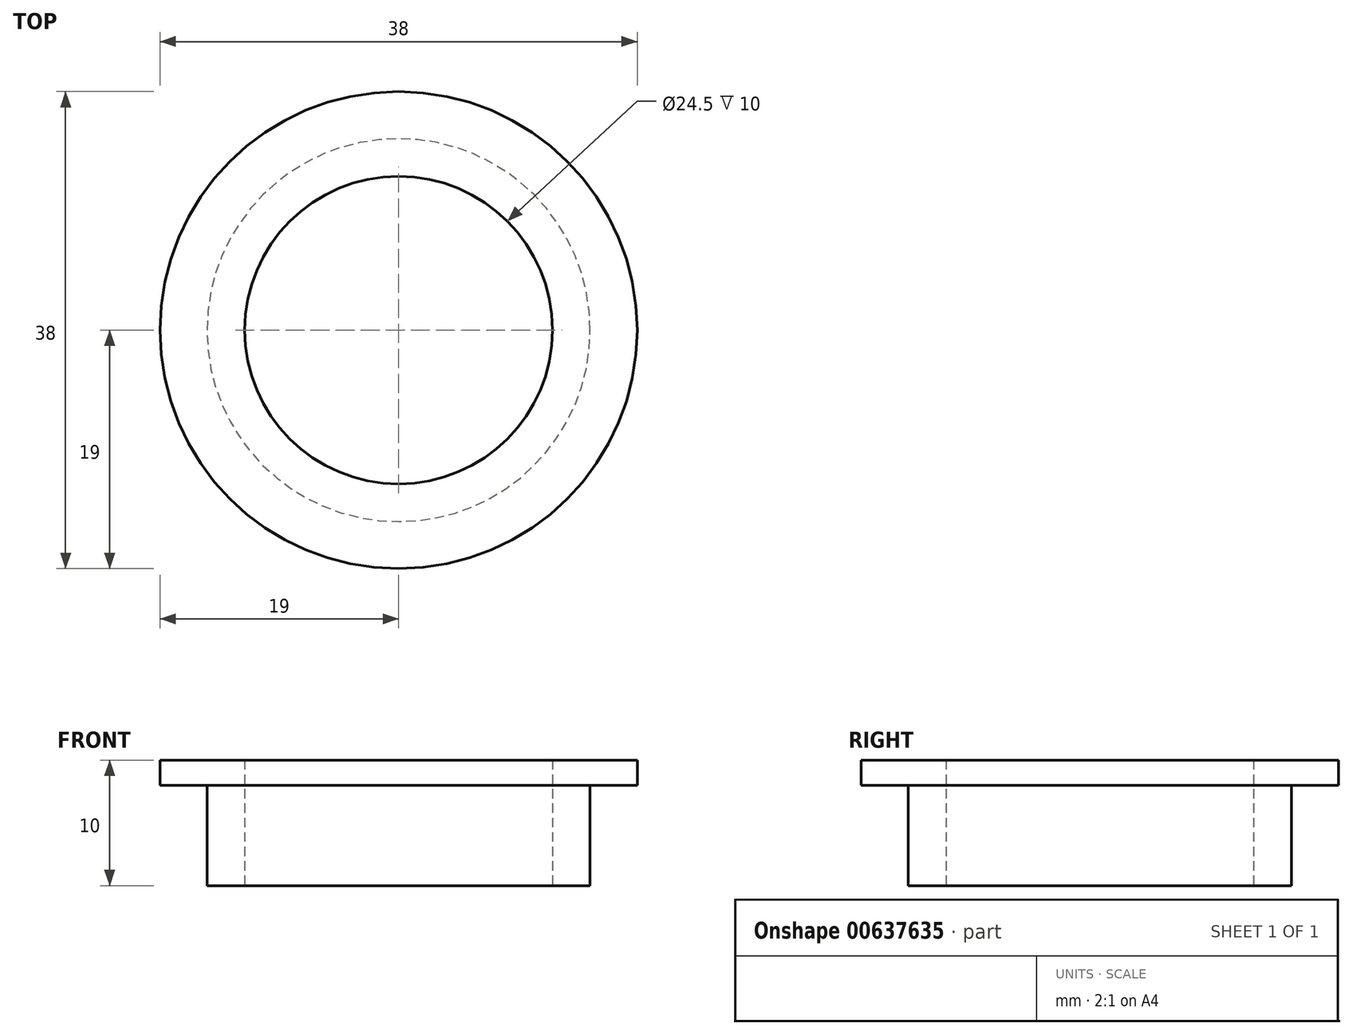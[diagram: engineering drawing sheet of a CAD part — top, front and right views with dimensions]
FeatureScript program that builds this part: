
annotation { "Feature Type Name" : "Feature", "Feature Type Description" : "" }
export const myFeature = defineFeature(function(context is Context, id is Id, definition is map)
    precondition{}
    {
        {
            var Q0;
            Q0=qCreatedBy(makeId("Top.planeOp"),FACE);
            var sketch = newSketch(context, id + "F0", { "sketchPlane" : qUnion([Q0])});
            skCircle(sketch, "E0", {"center": v(0, 0) * mm, "radius": 15.25 * mm});
            skCircle(sketch, "E1.0", {"center": v(0, 0) * mm, "radius": 12.25 * mm});
            skSolve(sketch);
        }
        {
            var Q0;
            Q0=makeQuery(id+"F0.imprint","IMPRINT",FACE,{"disambiguationData":[TD([[makeQuery(id+"F0.imprint","IMPRINT",EDGE,{"derivedFrom":sQuery(id+"F0.wireOp",EDGE,"E0")}),1.0]])]});
            extrude(context, id + "F1", {"entities" : qUnion([Q0]), "depth" : 10 * mm, "offsetDistance" : 25 * mm});
        }
        {
            var Q0;
            Q0=makeQuery(id+"F1.opExtrude","CAP_FACE",FACE,{"disambiguationData":[OSD([sQuery(id+"F0.wireOp",EDGE,"E0"),sQuery(id+"F0.wireOp",EDGE,"E1.0")])],"isStart":false});
            var sketch = newSketch(context, id + "F2", { "sketchPlane" : qUnion([Q0])});
            skCircle(sketch, "E2", {"center": v(0, 0) * mm, "radius": 19 * mm});
            skSolve(sketch);
        }
        {
            var Q0;
            Q0=makeQuery(id+"F2.imprint","IMPRINT",FACE,{"disambiguationData":[TD([[makeQuery(id+"F2.imprint","IMPRINT",EDGE,{"derivedFrom":sQuery(id+"F2.wireOp",EDGE,"E2")}),1.0]])]});
            extrude(context, id + "F3", {"entities" : qUnion([Q0]), "operationType" : NewBodyOperationType.ADD, "oppositeDirection" : true, "depth" : 2 * mm, "offsetDistance" : 25 * mm});
        }
    });
